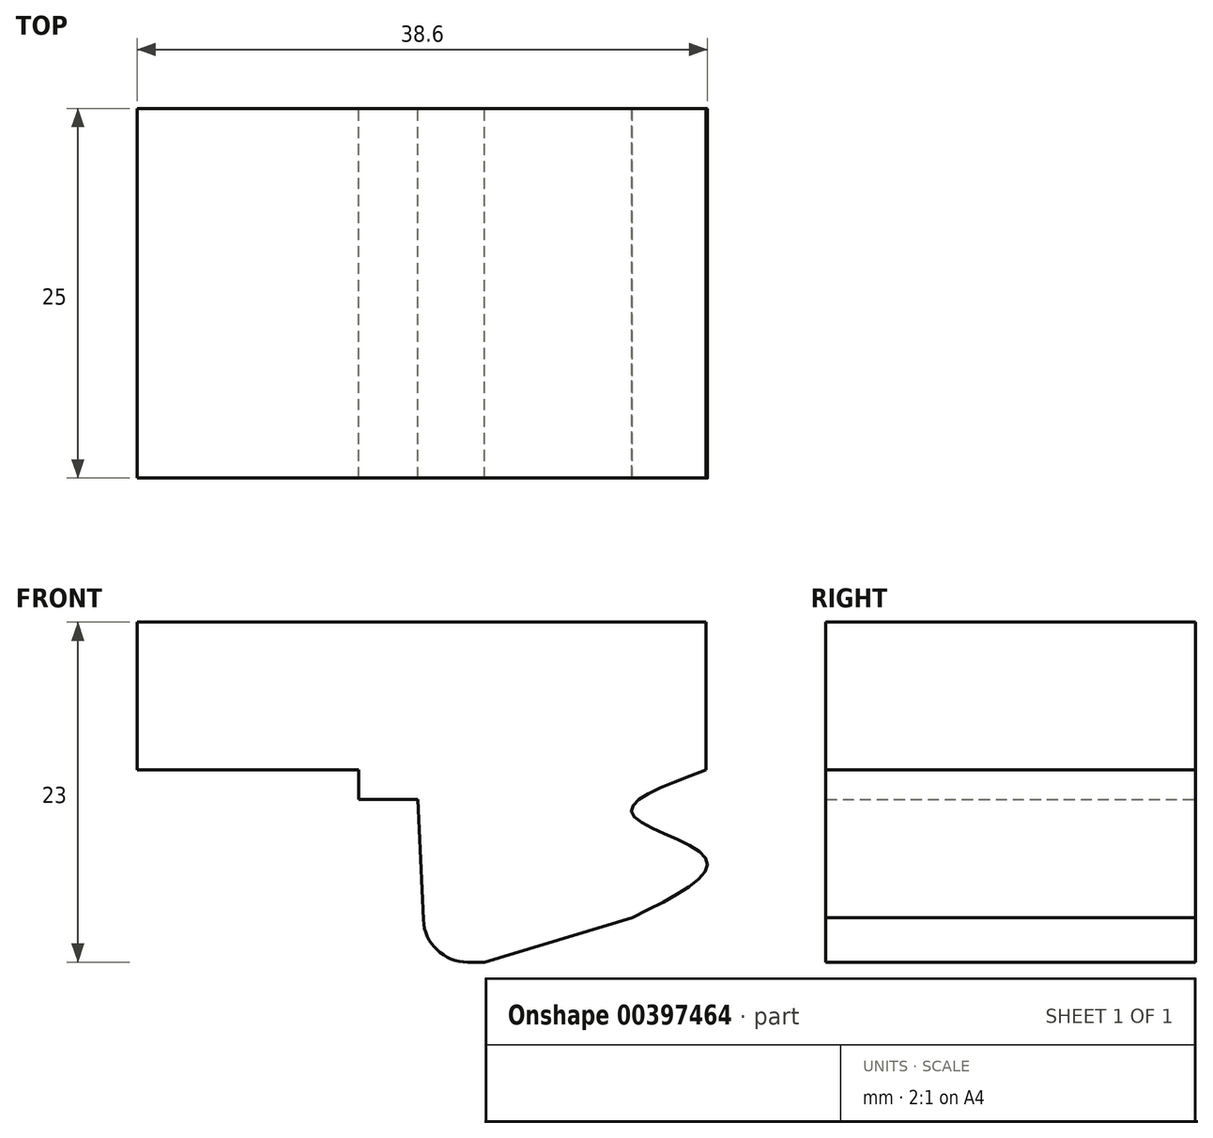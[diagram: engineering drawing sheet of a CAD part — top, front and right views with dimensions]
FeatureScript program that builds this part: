
annotation { "Feature Type Name" : "Feature", "Feature Type Description" : "" }
export const myFeature = defineFeature(function(context is Context, id is Id, definition is map)
    precondition{}
    {
        {
            var Q0;
            Q0=qCreatedBy(makeId("Front.planeOp"),FACE);
            var sketch = newSketch(context, id + "F0", { "sketchPlane" : qUnion([Q0])});
            skLineSegment(sketch, "E0", {"start": v(0, -4) * mm, "end": v(4, -4) * mm});
            skLineSegment(sketch, "E1", {"start": v(4, -4) * mm, "end": v(4, -4) * mm});
            skLineSegment(sketch, "E2", {"start": v(4, -4) * mm, "end": v(4.5, -4) * mm, "construction": true});
            skLineSegment(sketch, "E3", {"start": v(4.5, -4) * mm, "end": v(4.5, -15) * mm, "construction": true});
            skLineSegment(sketch, "E4", {"start": v(4, -4) * mm, "end": v(4.5, -15) * mm});
            skLineSegment(sketch, "E5", {"start": v(4.5, -15) * mm, "end": v(8.5, -15) * mm});
            skLineSegment(sketch, "E6", {"start": v(8.5, -15) * mm, "end": v(8.5, -12) * mm, "construction": true});
            skLineSegment(sketch, "E7", {"start": v(8.5, -12) * mm, "end": v(18.5, -12) * mm, "construction": true});
            skLineSegment(sketch, "E8", {"start": v(18.5, -12) * mm, "end": v(18.5, -5) * mm, "construction": true});
            skLineSegment(sketch, "E9", {"start": v(8.5, -15) * mm, "end": v(18.5, -12) * mm});
            skLineSegment(sketch, "E10", {"start": v(23.5, -2) * mm, "end": v(23.5, -5) * mm, "construction": true});
            skLineSegment(sketch, "E11", {"start": v(23.5, -5) * mm, "end": v(23.5, -8) * mm, "construction": true});
            skPoint(sketch, "E12.endSnap0", {"position": v(18.5, -8.5) * mm});
            skLineSegment(sketch, "E13", {"start": v(18.5, -5) * mm, "end": v(18.5, -5) * mm});
            skFitSpline(sketch, "E14", {"points": [v(23.5, -2) * mm, v(18.5, -5) * mm, v(23.5, -8) * mm, v(18.5, -12) * mm], "startDerivative": vector(-25.3, -9.3) * mm, "endDerivative": vector(-24.73, -12.31) * mm});
            skLineSegment(sketch, "E15", {"start": v(23.5, 8) * mm, "end": v(0, 8) * mm});
            skLineSegment(sketch, "E16", {"start": v(0, 8) * mm, "end": v(-15, 8) * mm});
            skLineSegment(sketch, "E17", {"start": v(-15, -2) * mm, "end": v(0, -2) * mm});
            skLineSegment(sketch, "E18", {"start": v(0, -2) * mm, "end": v(0, -4) * mm});
            skLineSegment(sketch, "E19", {"start": v(-15, -2) * mm, "end": v(-15, 0) * mm});
            skLineSegment(sketch, "E20", {"start": v(-15, 0) * mm, "end": v(-15, 8) * mm});
            skLineSegment(sketch, "E21", {"start": v(23.5, -2) * mm, "end": v(23.5, 0) * mm});
            skLineSegment(sketch, "E22", {"start": v(23.5, 0) * mm, "end": v(23.5, 8) * mm});
            skSolve(sketch);
        }
        {
            var Q0;
            Q0 = qSketchRegion(id + "F0", true);
            extrude(context, id + "F1", {"entities" : qUnion([Q0]), "endBound" : BoundingType.SYMMETRIC, "depth" : 25 * mm, "offsetDistance" : 25 * mm});
        }
        {
            var Q0;
            Q0=makeQuery(id+"F1.opExtrude","SWEPT_EDGE",EDGE,{"disambiguationData":[OSD([sQuery(id+"F0.wireOp",EDGE,"E4"),sQuery(id+"F0.wireOp",EDGE,"E5")])]});
            fillet(context, id + "F2", {"entities" : qUnion([Q0]), "radius" : 3 * mm, "tangentPropagation" : true, "allowEdgeOverflow" : false});
        }
    });
